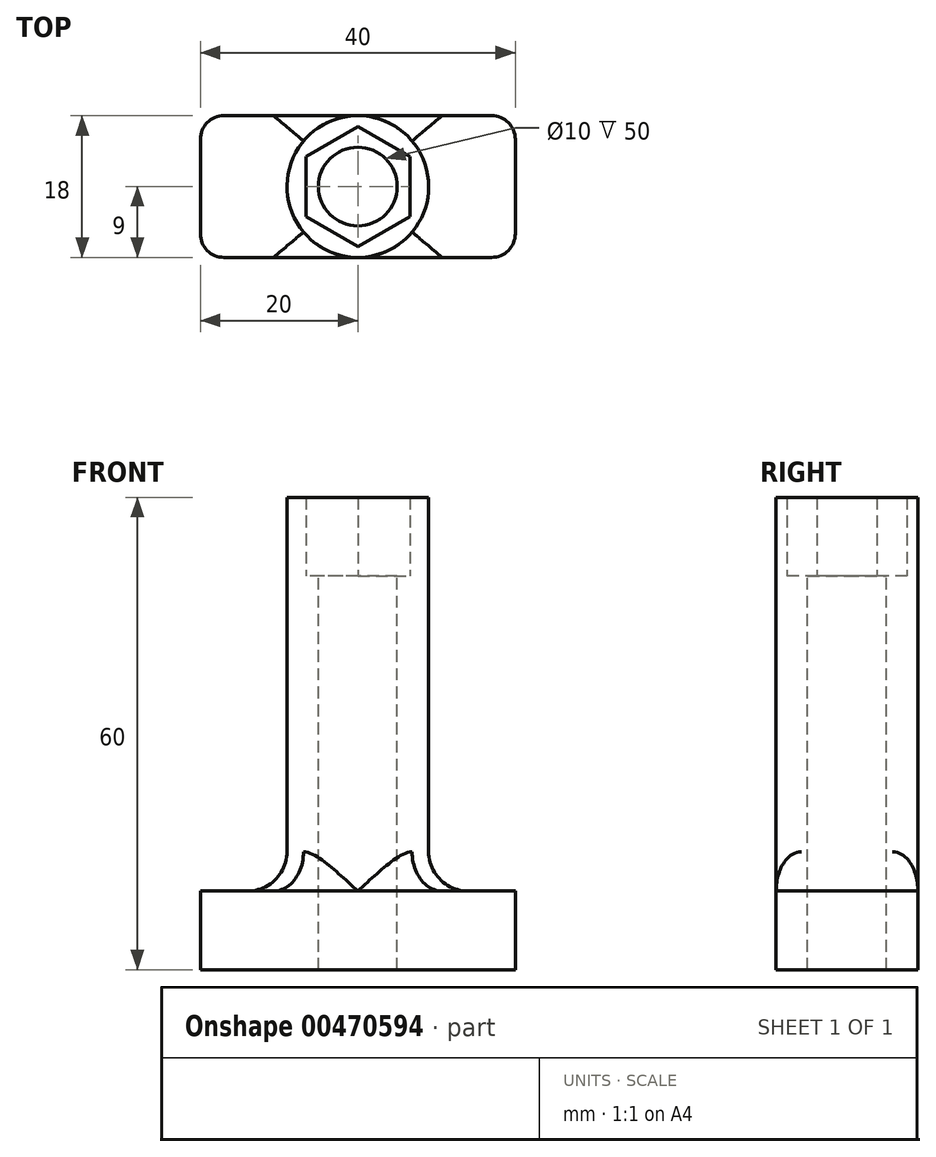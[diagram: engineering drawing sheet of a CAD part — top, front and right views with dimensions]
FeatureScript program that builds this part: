
annotation { "Feature Type Name" : "Feature", "Feature Type Description" : "" }
export const myFeature = defineFeature(function(context is Context, id is Id, definition is map)
    precondition{}
    {
        {
            var Q0;
            Q0=qCreatedBy(makeId("Top.planeOp"),FACE);
            var sketch = newSketch(context, id + "F0", { "sketchPlane" : qUnion([Q0])});
            skCircle(sketch, "E0.cCircle", {"center": v(0, 0) * mm, "radius": 6.6 * mm, "construction": true});
            skLineSegment(sketch, "E0.0", {"start": v(6.6, 3.81) * mm, "end": v(6.6, -3.81) * mm});
            skLineSegment(sketch, "E0.1", {"start": v(6.6, -3.81) * mm, "end": v(0, -7.62) * mm});
            skLineSegment(sketch, "E0.2", {"start": v(0, -7.62) * mm, "end": v(-6.6, -3.81) * mm});
            skLineSegment(sketch, "E0.3", {"start": v(-6.6, -3.81) * mm, "end": v(-6.6, 3.81) * mm});
            skLineSegment(sketch, "E0.4", {"start": v(-6.6, 3.81) * mm, "end": v(0, 7.62) * mm});
            skLineSegment(sketch, "E0.5", {"start": v(0, 7.62) * mm, "end": v(6.6, 3.81) * mm});
            skPoint(sketch, "E0.0.midPoint", {"position": v(6.6, 0) * mm});
            skCircle(sketch, "E1", {"center": v(0, 0) * mm, "radius": 9 * mm});
            skCircle(sketch, "E2", {"center": v(0, 0) * mm, "radius": 5 * mm});
            skPoint(sketch, "E3", {"position": v(0, 9) * mm});
            skLineSegment(sketch, "E4.bottom", {"start": v(20, 9) * mm, "end": v(-20, 9) * mm});
            skLineSegment(sketch, "E4.top", {"start": v(20, -9) * mm, "end": v(-20, -9) * mm});
            skLineSegment(sketch, "E4.left", {"start": v(20, 9) * mm, "end": v(20, -9) * mm});
            skLineSegment(sketch, "E4.right", {"start": v(-20, 9) * mm, "end": v(-20, -9) * mm});
            skSolve(sketch);
        }
        {
            var Q0;
            Q0=makeQuery(id+"F0.imprint","IMPRINT",FACE,{"disambiguationData":[TD([[makeQuery(id+"F0.imprint","IMPRINT",EDGE,{"derivedFrom":sQuery(id+"F0.wireOp",EDGE,"E0.0")}),1.0]])]});
            extrude(context, id + "F1", {"entities" : qUnion([Q0]), "depth" : 50 * mm});
        }
        {
            var Q0;
            Q0 = qSketchRegion(id + "F0", true);
            var Q1;
            Q1=makeQuery(id+"F0.imprint","IMPRINT",FACE,{"disambiguationData":[TD([[makeQuery(id+"F0.imprint","IMPRINT",EDGE,{"derivedFrom":sQuery(id+"F0.wireOp",EDGE,"E0.0")}),1.0]])]});
            var Q2;
            Q2=makeQuery(id+"F0.imprint","IMPRINT",FACE,{"disambiguationData":[TD([[makeQuery(id+"F0.imprint","IMPRINT",EDGE,{"derivedFrom":sQuery(id+"F0.wireOp",EDGE,"E0.0")}),-1.0]])]});
            extrude(context, id + "F2", {"entities" : qUnion([Q0, Q1, Q2]), "operationType" : NewBodyOperationType.ADD, "oppositeDirection" : true, "depth" : 10 * mm});
        }
        {
            var Q0;
            Q0=makeQuery(id+"F0.imprint","IMPRINT",FACE,{"disambiguationData":[TD([[makeQuery(id+"F0.imprint","IMPRINT",EDGE,{"derivedFrom":sQuery(id+"F0.wireOp",EDGE,"E0.0")}),-1.0]])]});
            extrude(context, id + "F3", {"entities" : qUnion([Q0]), "operationType" : NewBodyOperationType.ADD, "depth" : 40 * mm});
        }
        {
            var Q0;
            Q0=makeQuery(id+"F2.opExtrude","SWEPT_EDGE",EDGE,{"disambiguationData":[OSD([sQuery(id+"F0.wireOp",EDGE,"E4.top"),sQuery(id+"F0.wireOp",EDGE,"E4.right")])]});
            var Q1;
            Q1=makeQuery(id+"F2.opExtrude","SWEPT_EDGE",EDGE,{"disambiguationData":[OSD([sQuery(id+"F0.wireOp",EDGE,"E4.bottom"),sQuery(id+"F0.wireOp",EDGE,"E4.right")])]});
            var Q2;
            Q2=makeQuery(id+"F2.opExtrude","SWEPT_EDGE",EDGE,{"disambiguationData":[OSD([sQuery(id+"F0.wireOp",EDGE,"E4.bottom"),sQuery(id+"F0.wireOp",EDGE,"E4.left")])]});
            var Q3;
            Q3=makeQuery(id+"F2.opExtrude","SWEPT_EDGE",EDGE,{"disambiguationData":[OSD([sQuery(id+"F0.wireOp",EDGE,"E4.top"),sQuery(id+"F0.wireOp",EDGE,"E4.left")])]});
            fillet(context, id + "F4", {"entities" : qUnion([Q0, Q1, Q2, Q3]), "radius" : 3 * mm, "tangentPropagation" : true, "allowEdgeOverflow" : false});
        }
        {
            var Q0;
            Q0=makeQuery(id+"F2.boolean.opBoolean","SPLIT",EDGE,{"disambiguationData":[OD(0.0)],"derivedFrom":makeQuery(id+"F1.opExtrude","CAP_EDGE",EDGE,{"disambiguationData":[OSD([sQuery(id+"F0.wireOp",EDGE,"E1")])],"isStart":true})});
            fillet(context, id + "F5", {"entities" : qUnion([Q0]), "radius" : 5 * mm, "tangentPropagation" : true, "allowEdgeOverflow" : false});
        }
    });
